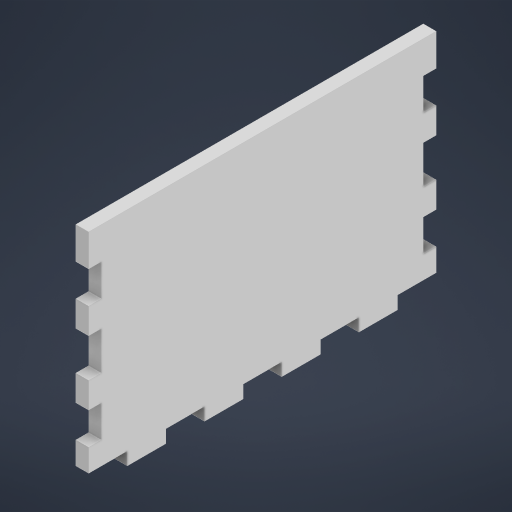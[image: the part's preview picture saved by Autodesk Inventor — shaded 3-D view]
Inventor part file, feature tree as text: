
AUTODESK INVENTOR PART (.ipt)
format: ipt  version: 2023.2 (Build 272271000, 271)  size: 282,112 bytes
history: native  units: mm
features: sketch x1
ambient origin geometry x8: Origin, YZ Plane, XZ Plane, XY Plane, X Axis, Y Axis, Z Axis, Center Point
bodies: Body1 (feature_tree)
feature tree (1):
  sketch  "Sketch1"  dims[d228=69.0mm d229=108.0mm d230=4.0mm d231=0.0mm d246=12.0mm d248=10.0mm d250=8.0mm d253=4.0mm d256=10.0mm d257=12.0mm d259=12.0mm d261=4.0mm d262=0.0mm d9=0.5mm d10=0.872665mm d11=0.5mm d12=0.872665mm d13=0.5mm d14=0.872665mm d27=0.5mm d28=0.872665mm d29=0.5mm d30=0.872665mm d88=0.5mm d89=0.872665mm d90=0.5mm d91=0.872665mm d116=0.5mm d117=0.872665mm d118=0.5mm d119=0.872665mm d154=0.5mm d155=0.872665mm d156=0.5mm d157=0.872665mm d181=0.5mm d182=0.872665mm d183=0.5mm d184=0.872665mm d221=0.5mm d222=0.872665mm d223=0.5mm d224=0.872665mm]
